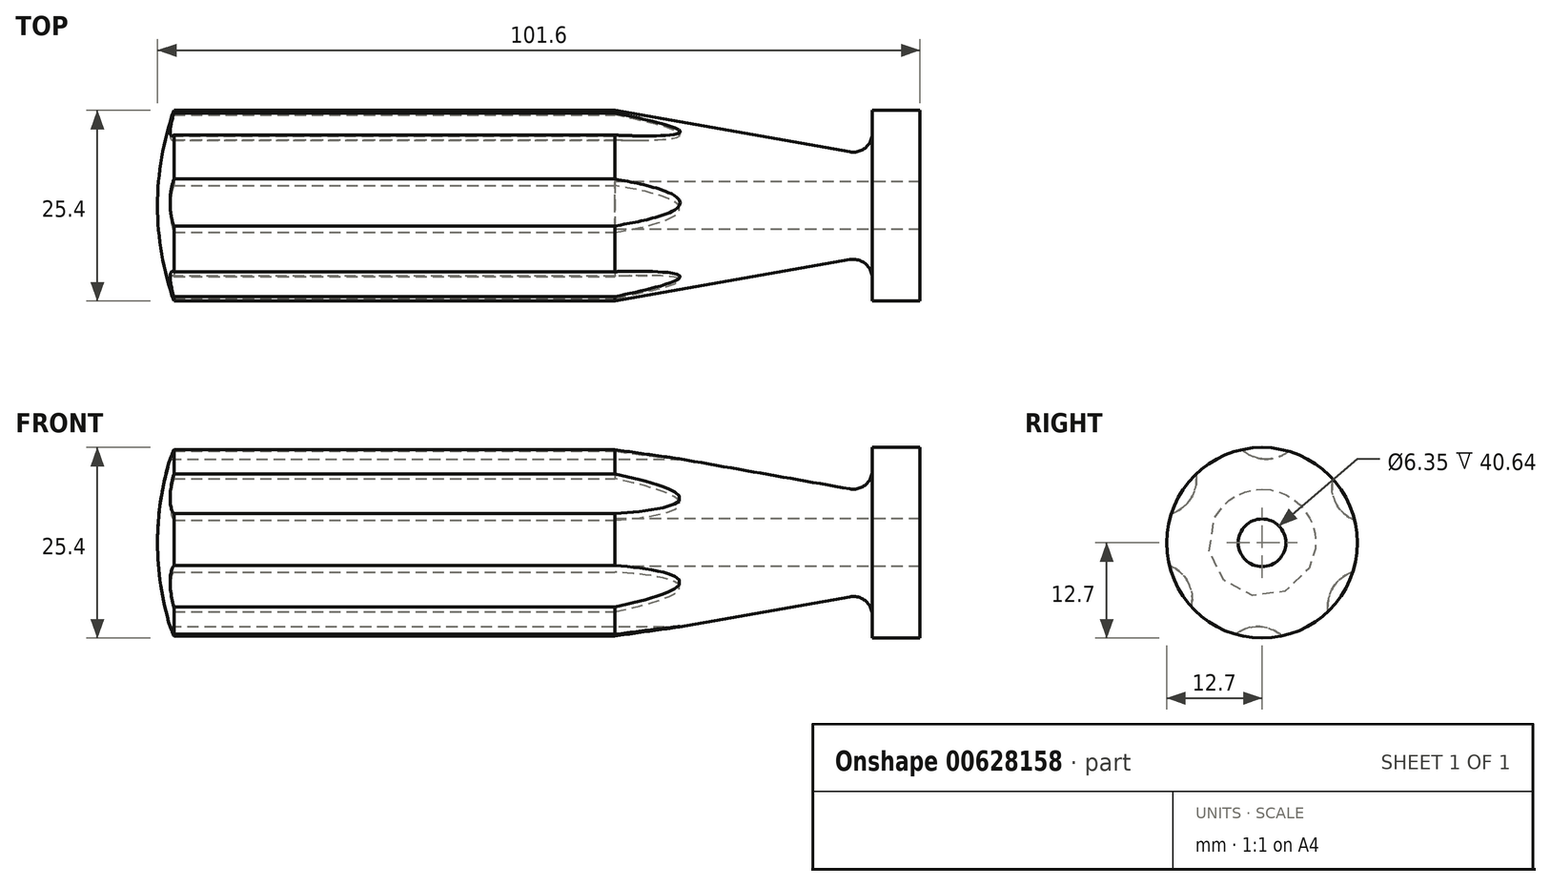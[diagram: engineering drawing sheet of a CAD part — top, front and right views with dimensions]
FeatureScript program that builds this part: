
annotation { "Feature Type Name" : "Feature", "Feature Type Description" : "" }
export const myFeature = defineFeature(function(context is Context, id is Id, definition is map)
    precondition{}
    {
        {
            var Q0;
            Q0=qCreatedBy(makeId("Front.planeOp"),FACE);
            var sketch = newSketch(context, id + "F0", { "sketchPlane" : qUnion([Q0])});
            skLineSegment(sketch, "E0", {"start": v(0, 7.16) * mm, "end": v(0, 12.7) * mm});
            skLineSegment(sketch, "E1", {"start": v(0, 12.7) * mm, "end": v(-6.35, 12.7) * mm});
            skLineSegment(sketch, "E2", {"start": v(-6.35, 12.7) * mm, "end": v(-6.35, 9.68) * mm});
            skLineSegment(sketch, "E3", {"start": v(-9.33, 7.18) * mm, "end": v(-40.64, 12.7) * mm});
            skLineSegment(sketch, "E4", {"start": v(-40.64, 12.7) * mm, "end": v(-99.42, 12.7) * mm});
            skLineSegment(sketch, "E5", {"start": v(-101.6, 0) * mm, "end": v(-40.64, 0) * mm});
            skLineSegment(sketch, "E6", {"start": v(-40.64, 0) * mm, "end": v(-40.64, 3.18) * mm});
            skLineSegment(sketch, "E7", {"start": v(-40.64, 3.18) * mm, "end": v(0, 3.18) * mm});
            skLineSegment(sketch, "E8", {"start": v(0, 3.18) * mm, "end": v(0, 7.16) * mm});
            skPoint(sketch, "E9.endSnap0", {"position": v(0, 9.93) * mm});
            skPoint(sketch, "E10.visualSharp", {"position": v(-6.35, 6.65) * mm});
            skArc(sketch, "E10.filletArc", {"start": v(-9.33, 7.18) * mm, "mid": v(-7.26, 7.74) * mm, "end": v(-6.35, 9.68) * mm});
            skArc(sketch, "E11.trimOffspring", {"start": v(-99.42, 12.7) * mm, "mid": v(-101.05, 6.44) * mm, "end": v(-101.6, 0) * mm});
            skSolve(sketch);
        }
        {
            var Q0;
            Q0 = qSketchRegion(id + "F0", true);
            var Q1;
            Q1=sQuery(id+"F0.wireOp",EDGE,"E5");
            revolve(context, id + "F1", {"entities" : qUnion([Q0]), "axis" : qUnion([Q1]), "revolveType" : RevolveType.FULL});
        }
        {
            var Q0;
            Q0=makeQuery(id+"F1.opRevolve","SWEPT_FACE",FACE,{"disambiguationData":[OSD([sQuery(id+"F0.wireOp",EDGE,"E0"),sQuery(id+"F0.wireOp",EDGE,"E8")])]});
            var sketch = newSketch(context, id + "F2", { "sketchPlane" : qUnion([Q0])});
            skCircle(sketch, "E12", {"center": v(0, 0) * mm, "radius": 16 * mm, "construction": true});
            skCircle(sketch, "E13", {"center": v(-14.13, -7.5) * mm, "radius": 4.83 * mm});
            skCircle(sketch, "E14.1.0", {"center": v(-13.56, 8.48) * mm, "radius": 4.83 * mm});
            skCircle(sketch, "E14.2.0", {"center": v(0.57, 15.98) * mm, "radius": 4.83 * mm});
            skCircle(sketch, "E14.3.0", {"center": v(14.13, 7.5) * mm, "radius": 4.83 * mm});
            skCircle(sketch, "E14.4.0", {"center": v(13.56, -8.48) * mm, "radius": 4.83 * mm});
            skCircle(sketch, "E14.5.0", {"center": v(-0.57, -15.98) * mm, "radius": 4.83 * mm});
            skLineSegment(sketch, "E14.anchor1", {"start": v(0, 0) * mm, "end": v(-14.13, -7.5) * mm, "construction": true});
            skLineSegment(sketch, "E14.anchor2", {"start": v(0, 0) * mm, "end": v(-0.57, -15.98) * mm, "construction": true});
            skSolve(sketch);
        }
        {
            var Q0;
            Q0 = qSketchRegion(id + "F2", true);
            extrude(context, id + "F3", {"entities" : qUnion([Q0]), "operationType" : NewBodyOperationType.REMOVE, "endBound" : BoundingType.THROUGH_ALL, "oppositeDirection" : true, "depth" : 25.4 * mm, "offsetDistance" : 25.4 * mm, "hasSecondDirection" : true, "secondDirectionOppositeDirection" : true, "secondDirectionDepth" : 7.62 * mm});
        }
    });
